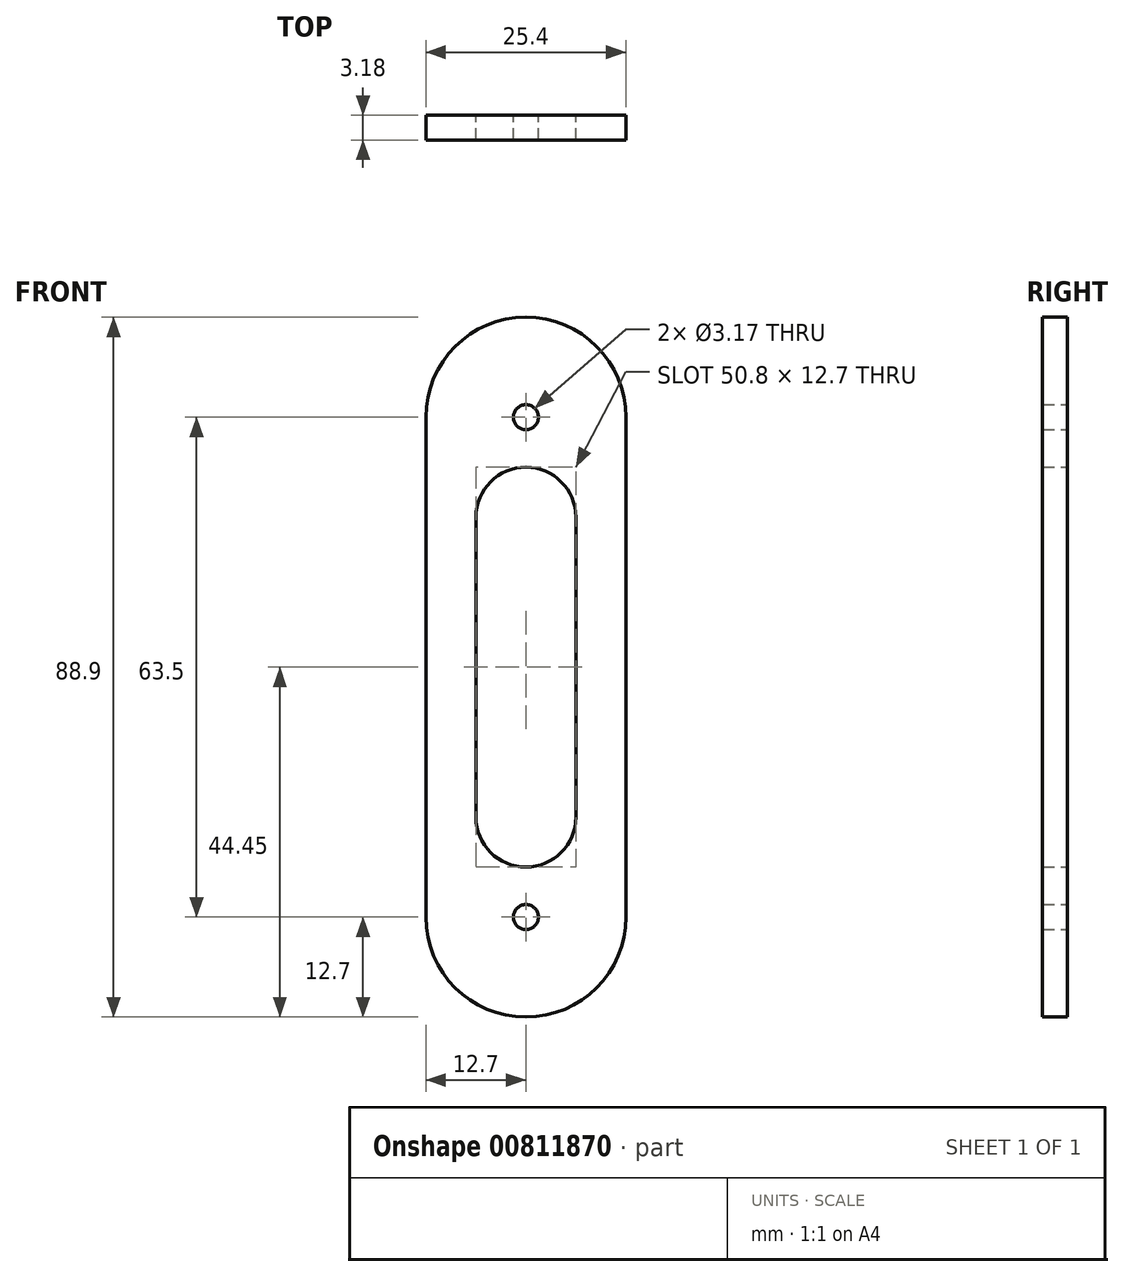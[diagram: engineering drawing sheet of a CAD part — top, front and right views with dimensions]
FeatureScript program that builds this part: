
annotation { "Feature Type Name" : "Feature", "Feature Type Description" : "" }
export const myFeature = defineFeature(function(context is Context, id is Id, definition is map)
    precondition{}
    {
        {
            var Q0;
            Q0=qCreatedBy(makeId("Front.planeOp"),FACE);
            var sketch = newSketch(context, id + "F0", { "sketchPlane" : qUnion([Q0])});
            skLineSegment(sketch, "E0.bottom", {"start": v(12.7, 0) * mm, "end": v(12.7, 0) * mm});
            skLineSegment(sketch, "E0.top", {"start": v(12.7, 88.9) * mm, "end": v(12.7, 88.9) * mm});
            skLineSegment(sketch, "E0.left", {"start": v(0, 12.7) * mm, "end": v(0, 76.2) * mm});
            skLineSegment(sketch, "E0.right", {"start": v(25.4, 12.7) * mm, "end": v(25.4, 76.2) * mm});
            skPoint(sketch, "E1.visualSharp", {"position": v(0, 88.9) * mm});
            skArc(sketch, "E1.filletArc", {"start": v(12.7, 88.9) * mm, "mid": v(3.72, 85.18) * mm, "end": v(0, 76.2) * mm});
            skPoint(sketch, "E2.visualSharp", {"position": v(25.4, 88.9) * mm});
            skArc(sketch, "E2.filletArc", {"start": v(25.4, 76.2) * mm, "mid": v(21.68, 85.18) * mm, "end": v(12.7, 88.9) * mm});
            skPoint(sketch, "E3.visualSharp", {"position": v(0, 0) * mm});
            skArc(sketch, "E3.filletArc", {"start": v(0, 12.7) * mm, "mid": v(3.72, 3.72) * mm, "end": v(12.7, 0) * mm});
            skPoint(sketch, "E4.visualSharp", {"position": v(25.4, 0) * mm});
            skArc(sketch, "E4.filletArc", {"start": v(12.7, 0) * mm, "mid": v(21.68, 3.72) * mm, "end": v(25.4, 12.7) * mm});
            skLineSegment(sketch, "E5.bottom", {"start": v(12.7, 69.85) * mm, "end": v(12.7, 69.85) * mm});
            skLineSegment(sketch, "E5.top", {"start": v(12.7, 19.05) * mm, "end": v(12.7, 19.05) * mm});
            skLineSegment(sketch, "E5.left", {"start": v(19.05, 63.5) * mm, "end": v(19.05, 25.4) * mm});
            skLineSegment(sketch, "E5.right", {"start": v(6.35, 63.5) * mm, "end": v(6.35, 25.4) * mm});
            skPoint(sketch, "E5.middle", {"position": v(12.7, 44.45) * mm});
            skPoint(sketch, "E6.visualSharp", {"position": v(6.35, 69.85) * mm});
            skArc(sketch, "E6.filletArc", {"start": v(12.7, 69.85) * mm, "mid": v(8.2, 68) * mm, "end": v(6.35, 63.5) * mm});
            skPoint(sketch, "E7.visualSharp", {"position": v(19.05, 69.85) * mm});
            skArc(sketch, "E7.filletArc", {"start": v(19.05, 63.5) * mm, "mid": v(17.2, 68) * mm, "end": v(12.7, 69.85) * mm});
            skPoint(sketch, "E8.visualSharp", {"position": v(6.35, 19.05) * mm});
            skArc(sketch, "E8.filletArc", {"start": v(6.35, 25.4) * mm, "mid": v(8.2, 20.9) * mm, "end": v(12.7, 19.05) * mm});
            skPoint(sketch, "E9.visualSharp", {"position": v(19.05, 19.05) * mm});
            skArc(sketch, "E9.filletArc", {"start": v(12.7, 19.05) * mm, "mid": v(17.2, 20.9) * mm, "end": v(19.05, 25.4) * mm});
            skLineSegment(sketch, "E10", {"start": v(12.7, 88.9) * mm, "end": v(12.7, 0) * mm});
            skCircle(sketch, "E11", {"center": v(12.7, 76.2) * mm, "radius": 1.59 * mm});
            skCircle(sketch, "E12", {"center": v(12.7, 12.7) * mm, "radius": 1.59 * mm});
            skSolve(sketch);
        }
        {
            var Q0;
            Q0 = qSketchRegion(id + "F0", true);
            extrude(context, id + "F1", {"entities" : qUnion([Q0]), "endBound" : BoundingType.SYMMETRIC, "depth" : 3.17 * mm, "offsetDistance" : 25.4 * mm});
        }
    });
